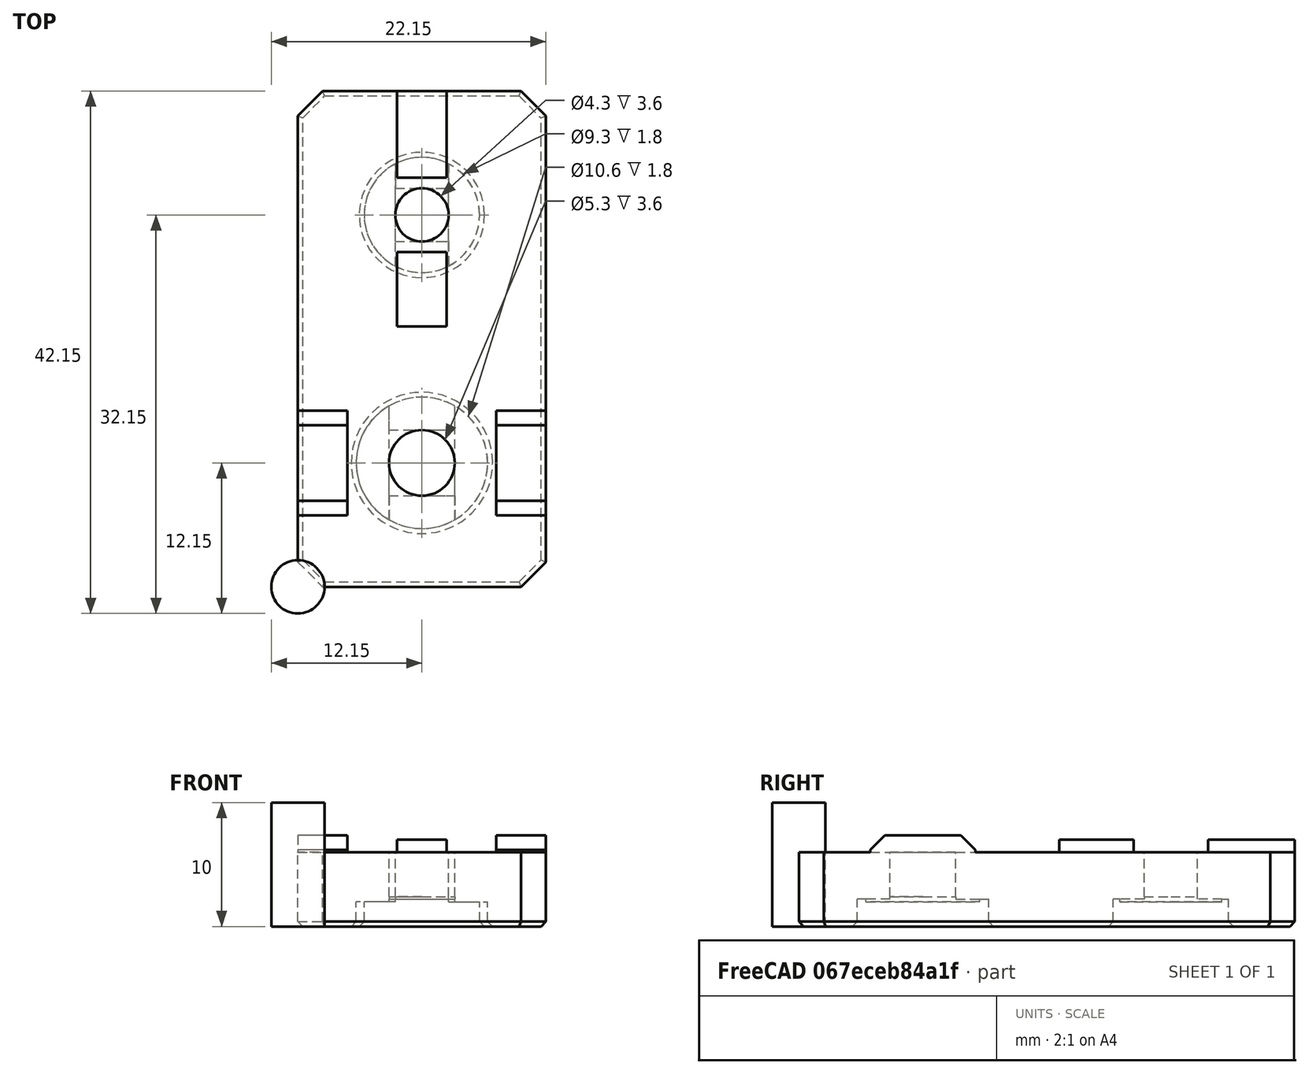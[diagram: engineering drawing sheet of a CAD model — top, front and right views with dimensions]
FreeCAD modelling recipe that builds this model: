
FCSTD DOCUMENT  (FreeCAD 0.18R14555 (Git shallow))
Label: rail-base-connector
License: All rights reserved
LicenseURL: http://en.wikipedia.org/wiki/All_rights_reserved
objects: Part::Box×12, Part::MultiFuse×6, Part::Cylinder×5, Part::Cut×5, Part::Feature×4, Part::Chamfer×2, Mesh::Feature×1
note: 34 computed .brp shape members not serialized (recipe doc carries the construction recipe); baked Part::Feature solids carry a one-line shape summary decoded from their .brp

FEATURE [Mesh::Feature] foot
FEATURE [Part::Feature] foot001
  shape: bbox 27.35 x 20 x 6 mm, 1212 faces, 0 solids (baked)
FEATURE [Part::Feature] foot001001  label="foot002"
  Placement = pos=(3.65,0,0) rot=(0,0,1;0rad)
  shape: bbox 27.35 x 20 x 6 mm, 382 faces, 0 solids (baked)
FEATURE [Part::Cylinder] Cylinder
  Angle = 360
  AttacherType = Attacher::AttachEngine3D
  Height = 10
  Placement = pos=(10,10,0) rot=(0,0,1;0rad)
  Radius = 2.65
FEATURE [Part::Box] Box  label="Cube"
  AttacherType = Attacher::AttachEngine3D
  Height = 6
  Length = 20
  Width = 40
FEATURE [Part::Cylinder] Cylinder001
  Angle = 360
  AttacherType = Attacher::AttachEngine3D
  Height = 10
  Placement = pos=(10,30,0) rot=(0,0,1;0rad)
  Radius = 2.15
FEATURE [Part::Feature] Part__Feature  label="v-slot-stablizer"
  Placement = pos=(26,20,5.95) rot=(0.707107,-0.707107,0;3.14159rad)
  shape: bbox 10 x 8.45 x 1.4 mm, 8 faces (baked)
FEATURE [Part::Feature] Part__Feature001  label="v-slot-stablizer001"
  Placement = pos=(36,20,5.95) rot=(0.707107,-0.707107,0;3.14159rad)
  shape: bbox 10 x 8.45 x 1.4 mm, 8 faces (baked)
FEATURE [Part::MultiFuse] Fusion
  Placement = pos=(0,0.995,0) rot=(0,0,1;0rad)
  Shapes = -> [Part__Feature,Part__Feature001]
FEATURE [Part::Box] Box001  label="Cube001"
  AttacherType = Attacher::AttachEngine3D
  Height = 1
  Length = 4
  Placement = pos=(8,21,6) rot=(0,0,1;0rad)
  Width = 6
FEATURE [Part::Box] Box002  label="Cube002"
  AttacherType = Attacher::AttachEngine3D
  Height = 0.4
  Length = 5
  Placement = pos=(2.35,5,0) rot=(0,0,1;0rad)
  Width = 10
FEATURE [Part::Box] Box003  label="Cube003"
  AttacherType = Attacher::AttachEngine3D
  Height = 0.4
  Length = 5
  Placement = pos=(12.65,5,0) rot=(0,0,1;0rad)
  Width = 10
FEATURE [Part::Box] Box004  label="Cube004"
  AttacherType = Attacher::AttachEngine3D
  Height = 0.2
  Length = 10
  Placement = pos=(5,2.35,0.2) rot=(0,0,1;0rad)
  Width = 5
FEATURE [Part::Box] Box005  label="Cube005"
  AttacherType = Attacher::AttachEngine3D
  Height = 0.2
  Length = 10
  Placement = pos=(5,12.65,0.2) rot=(0,0,1;0rad)
  Width = 5
FEATURE [Part::MultiFuse] Fusion002
  Placement = pos=(0,0,2) rot=(0,0,1;0rad)
  Shapes = -> [Box005,Box003,Box002,Box004]
FEATURE [Part::Cylinder] Cylinder002
  Angle = 360
  AttacherType = Attacher::AttachEngine3D
  Height = 2.4
  Placement = pos=(10,10,0) rot=(0,0,1;0rad)
  Radius = 5.3
FEATURE [Part::Cylinder] Cylinder003
  Angle = 360
  AttacherType = Attacher::AttachEngine3D
  Height = 2.4
  Placement = pos=(10,30,0) rot=(0,0,1;0rad)
  Radius = 4.65
FEATURE [Part::Cylinder] Cylinder004
  Angle = 360
  AttacherType = Attacher::AttachEngine3D
  Height = 10
  Radius = 2.15
FEATURE [Part::Box] Box006  label="Cube006"
  AttacherType = Attacher::AttachEngine3D
  Height = 0.4
  Length = 5
  Placement = pos=(2.15,-5,0) rot=(0,0,1;0rad)
  Width = 10
FEATURE [Part::Box] Box007  label="Cube007"
  AttacherType = Attacher::AttachEngine3D
  Height = 0.4
  Length = 5
  Placement = pos=(-7.15,-5,0) rot=(0,0,1;0rad)
  Width = 10
FEATURE [Part::Box] Box008  label="Cube008"
  AttacherType = Attacher::AttachEngine3D
  Height = 0.2
  Length = 10
  Placement = pos=(-5,2.15,0.2) rot=(0,0,1;0rad)
  Width = 5
FEATURE [Part::Box] Box009  label="Cube009"
  AttacherType = Attacher::AttachEngine3D
  Height = 0.2
  Length = 10
  Placement = pos=(-5,-7.15,0.2) rot=(0,0,1;0rad)
  Width = 5
FEATURE [Part::MultiFuse] Fusion003
  Placement = pos=(10,30,2) rot=(0,0,1;0rad)
  Shapes = -> [Box006,Box009,Box007,Box008]
FEATURE [Part::Box] Box010  label="Cube010"
  AttacherType = Attacher::AttachEngine3D
  Height = 1
  Length = 4
  Placement = pos=(8,33,6) rot=(0,0,1;0rad)
  Width = 7
FEATURE [Part::MultiFuse] Fusion004
  Shapes = -> [Fusion,Box,Box001,Box010]
FEATURE [Part::Cut] Cut
  Base = -> Fusion004
  Tool = -> Cylinder
FEATURE [Part::Cut] Cut001
  Base = -> Cut
  Tool = -> Cylinder001
FEATURE [Part::Cut] Cut002
  Base = -> Cut001
  Tool = -> Cylinder002
FEATURE [Part::Cut] Cut003
  Base = -> Cut002
  Tool = -> Cylinder003
FEATURE [Part::MultiFuse] Fusion005
  Shapes = -> [Cut003,Fusion002]
FEATURE [Part::MultiFuse] Fusion006
  Shapes = -> [Fusion005,Fusion003]
FEATURE [Part::Chamfer] Chamfer
  Base = -> Fusion006
  Edges = 4 edges r=2: [Edge6,Edge8,Edge28,Edge34]
FEATURE [Part::Chamfer] Chamfer001
  Base = -> Chamfer
  Edges = 10 edges r=0.4: [Edge4,Edge15,Edge18,Edge19,Edge20,Edge21,Edge22,Edge23,Edge24,Edge25]
FEATURE [Part::Box] Box011  label="Cube011"
  AttacherType = Attacher::AttachEngine3D
  Height = 10
  Length = 12
  Placement = pos=(4,5,6) rot=(0,0,1;0rad)
  Width = 10
FEATURE [Part::Cut] Cut004
  Base = -> Chamfer001
  Tool = -> Box011
